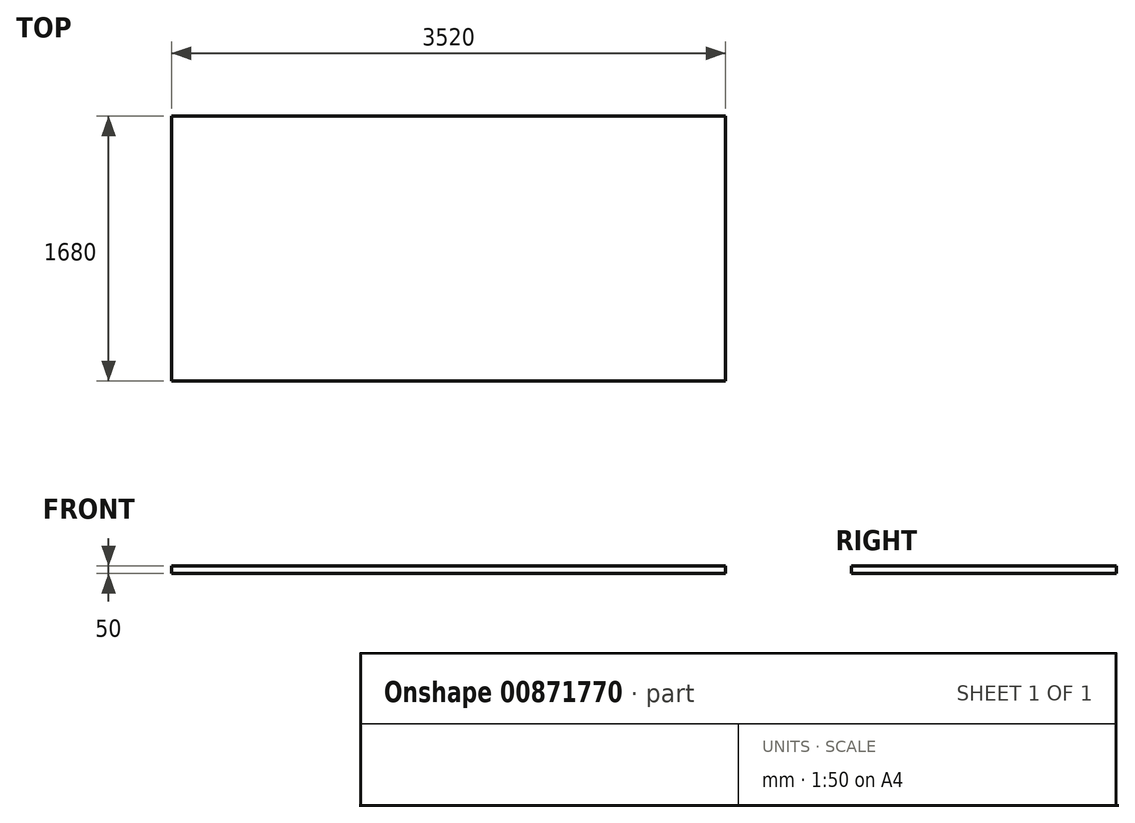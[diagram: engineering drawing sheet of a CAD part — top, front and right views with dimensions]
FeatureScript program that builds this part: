
annotation { "Feature Type Name" : "Feature", "Feature Type Description" : "" }
export const myFeature = defineFeature(function(context is Context, id is Id, definition is map)
    precondition{}
    {
        {
            var Q0;
            Q0=qCreatedBy(makeId("Top.planeOp"),FACE);
            var sketch = newSketch(context, id + "F0", { "sketchPlane" : qUnion([Q0])});
            skLineSegment(sketch, "E0.bottom", {"start": v(1760, -840) * mm, "end": v(-1760, -840) * mm});
            skLineSegment(sketch, "E0.top", {"start": v(1760, 840) * mm, "end": v(-1760, 840) * mm});
            skLineSegment(sketch, "E0.left", {"start": v(1760, -840) * mm, "end": v(1760, 840) * mm});
            skLineSegment(sketch, "E0.right", {"start": v(-1760, -840) * mm, "end": v(-1760, 840) * mm});
            skPoint(sketch, "E0.middle", {"position": v(0, 0) * mm});
            skSolve(sketch);
        }
        {
            var Q0;
            Q0=makeQuery(id+"F0.imprint","IMPRINT",FACE,{"disambiguationData":[TD([[makeQuery(id+"F0.imprint","IMPRINT",EDGE,{"derivedFrom":sQuery(id+"F0.wireOp",EDGE,"E0.bottom")}),-1.0]])]});
            extrude(context, id + "F1", {"entities" : qUnion([Q0]), "depth" : 50 * mm, "offsetDistance" : 25 * mm});
        }
    });
